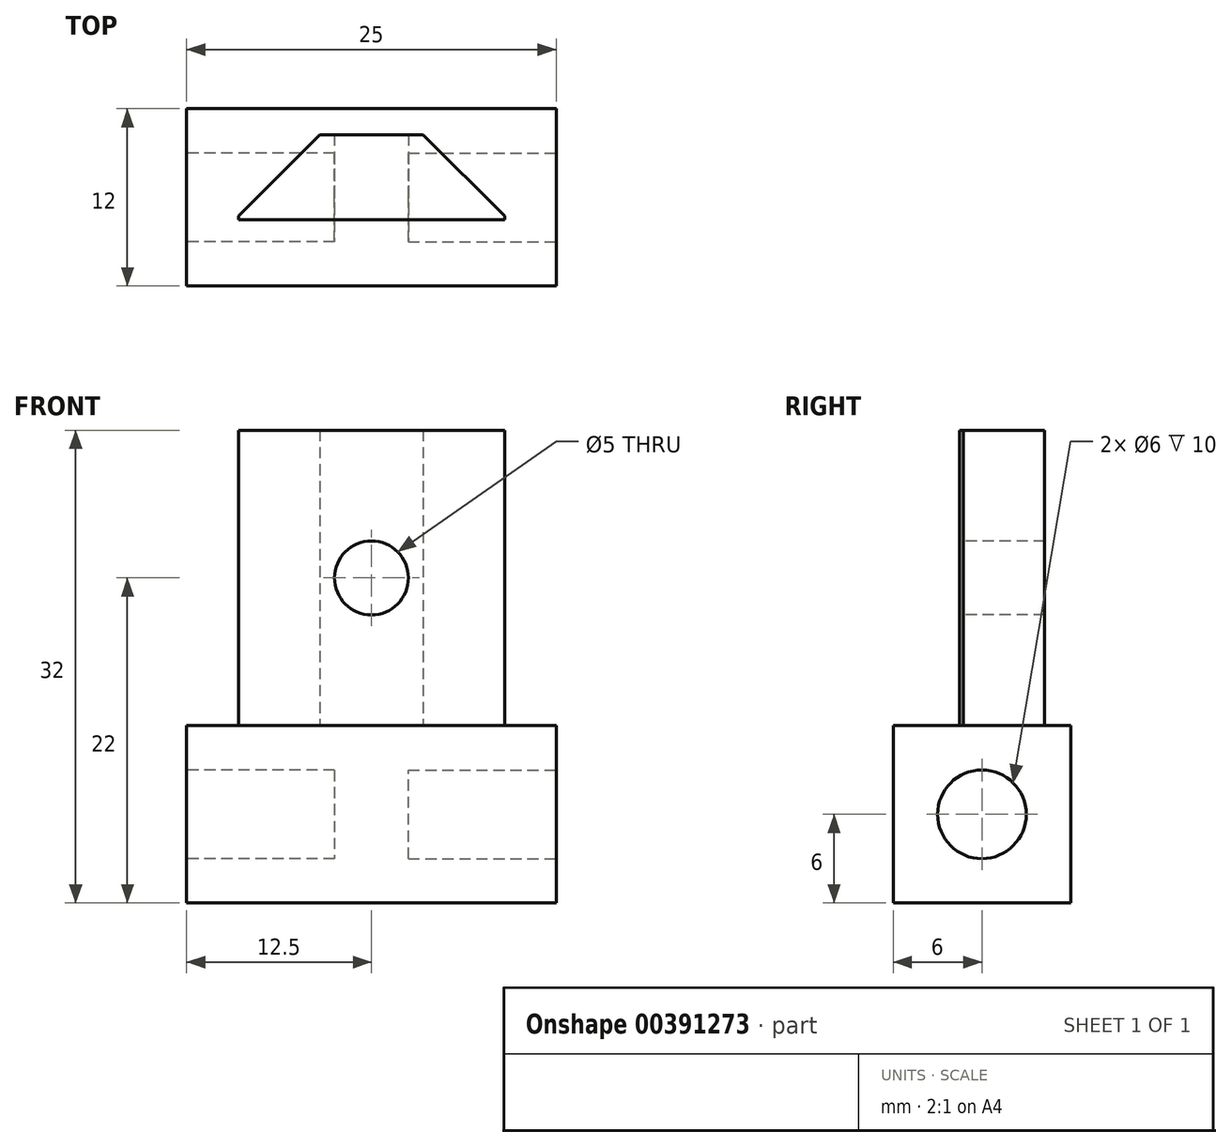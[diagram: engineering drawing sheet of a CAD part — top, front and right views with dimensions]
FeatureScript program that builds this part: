
annotation { "Feature Type Name" : "Feature", "Feature Type Description" : "" }
export const myFeature = defineFeature(function(context is Context, id is Id, definition is map)
    precondition{}
    {
        {
            var Q0;
            Q0=qCreatedBy(makeId("Top.planeOp"),FACE);
            var sketch = newSketch(context, id + "F0", { "sketchPlane" : qUnion([Q0])});
            skLineSegment(sketch, "E0", {"start": v(0, 0) * mm, "end": v(9, 0) * mm});
            skLineSegment(sketch, "E1", {"start": v(9, 0) * mm, "end": v(9, 0.25) * mm});
            skLineSegment(sketch, "E2", {"start": v(9, 0.25) * mm, "end": v(3.5, 5.75) * mm});
            skLineSegment(sketch, "E3", {"start": v(3.5, 5.75) * mm, "end": v(0, 5.75) * mm});
            skLineSegment(sketch, "E4.MirrorCS", {"start": v(-9, 0) * mm, "end": v(-9, 0.25) * mm});
            skLineSegment(sketch, "E5.MirrorCS", {"start": v(-9, 0.25) * mm, "end": v(-3.5, 5.75) * mm});
            skLineSegment(sketch, "E6.MirrorCS", {"start": v(-3.5, 5.75) * mm, "end": v(0, 5.75) * mm});
            skLineSegment(sketch, "E7.MirrorCS", {"start": v(0, 0) * mm, "end": v(-9, 0) * mm});
            skSolve(sketch);
        }
        {
            var Q0;
            Q0=makeQuery(id+"F0.imprint","IMPRINT",FACE,{"disambiguationData":[TD([[makeQuery(id+"F0.imprint","IMPRINT",EDGE,{"derivedFrom":sQuery(id+"F0.wireOp",EDGE,"E0")}),1.0]])]});
            extrude(context, id + "F1", {"entities" : qUnion([Q0]), "depth" : 20 * mm, "offsetDistance" : 25 * mm});
        }
        {
            var Q0;
            Q0=qCreatedBy(makeId("Top.planeOp"),FACE);
            var sketch = newSketch(context, id + "F2", { "sketchPlane" : qUnion([Q0])});
            skLineSegment(sketch, "E8.bottom", {"start": v(-12.5, -4.5) * mm, "end": v(12.5, -4.5) * mm});
            skLineSegment(sketch, "E8.top", {"start": v(-12.5, 7.5) * mm, "end": v(12.5, 7.5) * mm});
            skLineSegment(sketch, "E8.left", {"start": v(-12.5, -4.5) * mm, "end": v(-12.5, 7.5) * mm});
            skLineSegment(sketch, "E8.right", {"start": v(12.5, -4.5) * mm, "end": v(12.5, 7.5) * mm});
            skSolve(sketch);
        }
        {
            var Q0;
            Q0=makeQuery(id+"F2.imprint","IMPRINT",FACE,{"disambiguationData":[TD([[makeQuery(id+"F2.imprint","IMPRINT",EDGE,{"derivedFrom":sQuery(id+"F2.wireOp",EDGE,"E8.bottom")}),1.0]])]});
            extrude(context, id + "F3", {"entities" : qUnion([Q0]), "operationType" : NewBodyOperationType.ADD, "oppositeDirection" : true, "depth" : 12 * mm, "offsetDistance" : 25 * mm});
        }
        {
            var Q0;
            Q0=makeQuery(id+"F3.opExtrude","SWEPT_FACE",FACE,{"disambiguationData":[OSD([sQuery(id+"F2.wireOp",EDGE,"E8.right")])]});
            var sketch = newSketch(context, id + "F4", { "sketchPlane" : qUnion([Q0])});
            skCircle(sketch, "E9", {"center": v(1.5, -6) * mm, "radius": 3 * mm});
            skPoint(sketch, "E9.centerSnap0", {"position": v(7.5, -6) * mm});
            skPoint(sketch, "E9.centerSnap1", {"position": v(1.5, -12) * mm});
            skSolve(sketch);
        }
        {
            var Q0;
            Q0=makeQuery(id+"F4.imprint","IMPRINT",FACE,{"disambiguationData":[TD([[makeQuery(id+"F4.imprint","IMPRINT",EDGE,{"derivedFrom":sQuery(id+"F4.wireOp",EDGE,"E9")}),1.0]])]});
            extrude(context, id + "F5", {"entities" : qUnion([Q0]), "operationType" : NewBodyOperationType.REMOVE, "oppositeDirection" : true, "depth" : 10 * mm, "offsetDistance" : 25 * mm});
        }
        {
            var Q0;
            Q0=makeQuery(id+"F3.opExtrude","SWEPT_FACE",FACE,{"disambiguationData":[OSD([sQuery(id+"F2.wireOp",EDGE,"E8.left")])]});
            var sketch = newSketch(context, id + "F6", { "sketchPlane" : qUnion([Q0])});
            skCircle(sketch, "E10", {"center": v(-1.5, -6) * mm, "radius": 3 * mm});
            skPoint(sketch, "E10.centerSnap0", {"position": v(4.5, -6) * mm});
            skPoint(sketch, "E10.centerSnap1", {"position": v(-1.5, -12) * mm});
            skSolve(sketch);
        }
        {
            var Q0;
            Q0=makeQuery(id+"F6.imprint","IMPRINT",FACE,{"disambiguationData":[TD([[makeQuery(id+"F6.imprint","IMPRINT",EDGE,{"derivedFrom":sQuery(id+"F6.wireOp",EDGE,"E10")}),1.0]])]});
            extrude(context, id + "F7", {"entities" : qUnion([Q0]), "operationType" : NewBodyOperationType.REMOVE, "oppositeDirection" : true, "depth" : 10 * mm, "offsetDistance" : 25 * mm});
        }
        {
            var Q0;
            Q0=makeQuery(id+"F1.opExtrude","SWEPT_FACE",FACE,{"disambiguationData":[OSD([sQuery(id+"F0.wireOp",EDGE,"E0"),sQuery(id+"F0.wireOp",EDGE,"E7.MirrorCS")])]});
            var sketch = newSketch(context, id + "F8", { "sketchPlane" : qUnion([Q0])});
            skCircle(sketch, "E11", {"center": v(0, 10) * mm, "radius": 2.5 * mm});
            skPoint(sketch, "E11.centerSnap0", {"position": v(0, 20) * mm});
            skPoint(sketch, "E11.centerSnap1", {"position": v(-9, 10) * mm});
            skSolve(sketch);
        }
        {
            var Q0;
            Q0=makeQuery(id+"F8.imprint","IMPRINT",FACE,{"disambiguationData":[TD([[makeQuery(id+"F8.imprint","IMPRINT",EDGE,{"derivedFrom":sQuery(id+"F8.wireOp",EDGE,"E11")}),1.0]])]});
            extrude(context, id + "F9", {"entities" : qUnion([Q0]), "operationType" : NewBodyOperationType.REMOVE, "oppositeDirection" : true, "depth" : 25 * mm, "offsetDistance" : 25 * mm});
        }
    });
